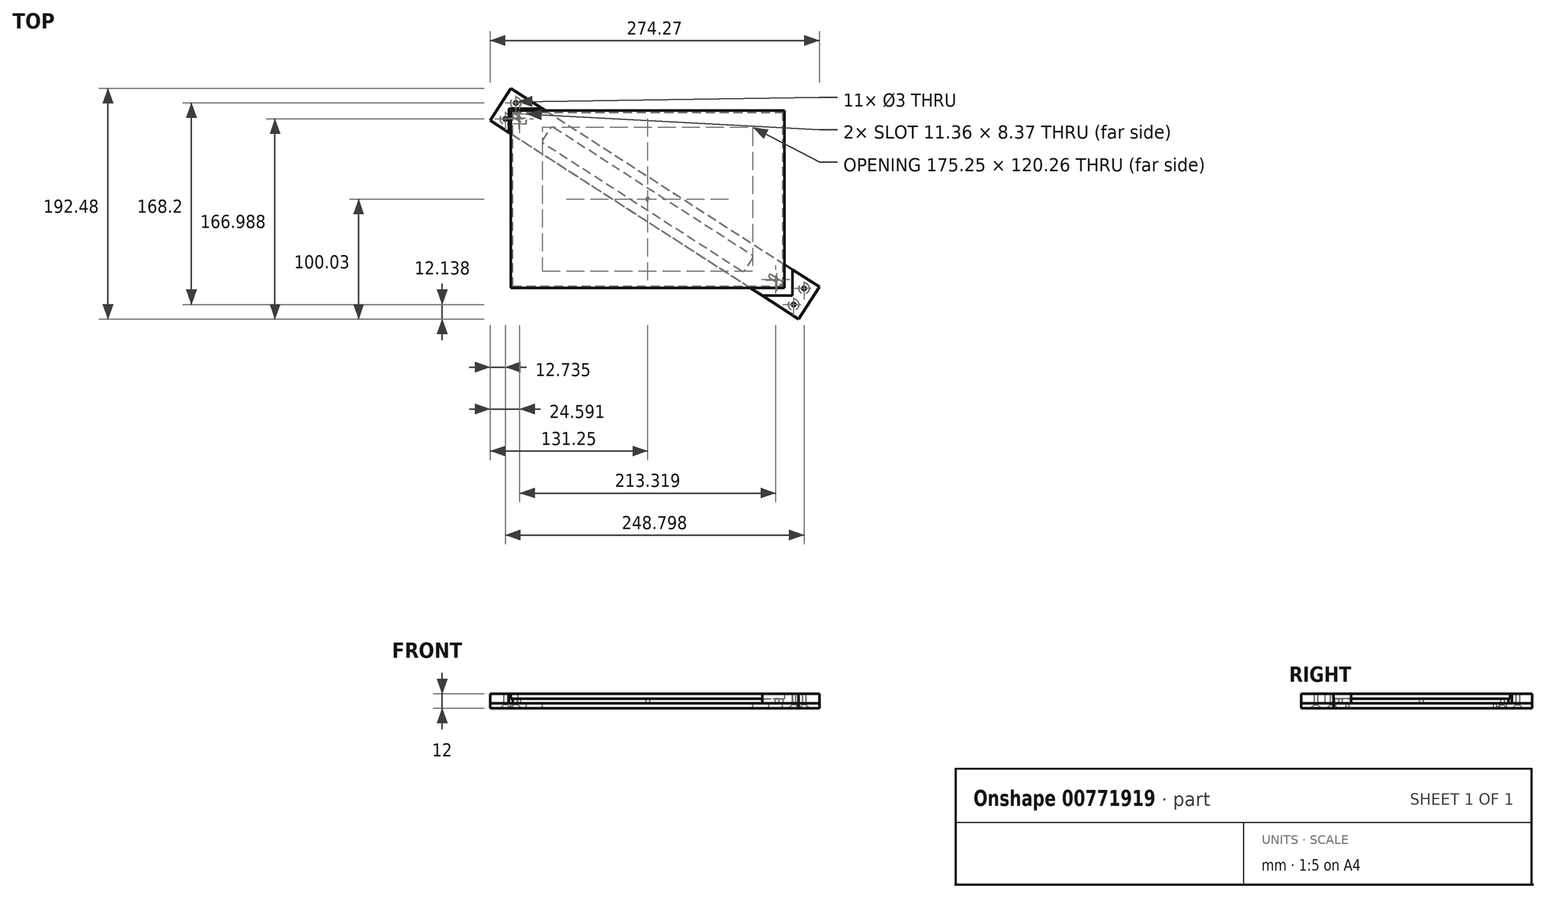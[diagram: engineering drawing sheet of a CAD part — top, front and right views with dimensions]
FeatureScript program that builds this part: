
annotation { "Feature Type Name" : "Feature", "Feature Type Description" : "" }
export const myFeature = defineFeature(function(context is Context, id is Id, definition is map)
    precondition{}
    {
        {
            assignVariable(context, id + "F0", {"name" : "printPlateThickness", "anyValue" : 4 * mm});
        }
        {
            var Q0;
            Q0=qCreatedBy(makeId("Top.planeOp"),FACE);
            var sketch = newSketch(context, id + "F1", { "sketchPlane" : qUnion([Q0])});
            skLineSegment(sketch, "E0.bottom", {"start": v(0, 0) * mm, "end": v(225, 0) * mm});
            skLineSegment(sketch, "E0.top", {"start": v(0, 145) * mm, "end": v(225, 145) * mm});
            skLineSegment(sketch, "E0.left", {"start": v(0, 0) * mm, "end": v(0, 145) * mm});
            skLineSegment(sketch, "E0.right", {"start": v(225, 0) * mm, "end": v(225, 145) * mm});
            skCircle(sketch, "E1", {"center": v(5, 140) * mm, "radius": 1.5 * mm});
            skCircle(sketch, "E2", {"center": v(220, 5) * mm, "radius": 1.5 * mm});
            skLineSegment(sketch, "E3.bottom", {"start": v(-1.5, 146.5) * mm, "end": v(226.5, 146.5) * mm});
            skLineSegment(sketch, "E3.top", {"start": v(-1.5, -1.5) * mm, "end": v(226.5, -1.5) * mm});
            skLineSegment(sketch, "E3.left", {"start": v(-1.5, 146.5) * mm, "end": v(-1.5, -1.5) * mm});
            skLineSegment(sketch, "E3.right", {"start": v(226.5, 146.5) * mm, "end": v(226.5, -1.5) * mm});
            skLineSegment(sketch, "E4", {"start": v(0, 0) * mm, "end": v(225, 145) * mm, "construction": true});
            skLineSegment(sketch, "E5", {"start": v(0, 145) * mm, "end": v(225, 0) * mm, "construction": true});
            skCircle(sketch, "E6", {"center": v(112.5, 72.5) * mm, "radius": 1.5 * mm});
            skSolve(sketch);
        }
        {
            var Q0;
            Q0=makeQuery(id+"F1.imprint","IMPRINT",FACE,{"disambiguationData":[TD([[makeQuery(id+"F1.imprint","IMPRINT",EDGE,{"derivedFrom":sQuery(id+"F1.wireOp",EDGE,"E0.bottom")}),1.0]])]});
            extrude(context, id + "F2", {"entities" : qUnion([Q0]), "depth" : getVariable(context, 'printPlateThickness'), "offsetDistance" : 25 * mm});
        }
        {
            var Q0;
            Q0=qCreatedBy(makeId("Top.planeOp"),FACE);
            var sketch = newSketch(context, id + "F3", { "sketchPlane" : qUnion([Q0])});
            skLineSegment(sketch, "E7", {"start": v(0, 145) * mm, "end": v(225, 0) * mm, "construction": true});
            skLineSegment(sketch, "E8", {"start": v(225, 0) * mm, "end": v(246.85, -14.08) * mm, "construction": true});
            skLineSegment(sketch, "E9", {"start": v(0, 145) * mm, "end": v(-10.09, 151.5) * mm, "construction": true});
            skLineSegment(sketch, "E10", {"start": v(-18.75, 138.05) * mm, "end": v(-1.42, 164.95) * mm});
            skLineSegment(sketch, "E11", {"start": v(-1.42, 164.95) * mm, "end": v(255.52, -0.64) * mm});
            skLineSegment(sketch, "E12", {"start": v(255.52, -0.64) * mm, "end": v(238.19, -27.53) * mm});
            skLineSegment(sketch, "E13", {"start": v(238.19, -27.53) * mm, "end": v(-18.75, 138.05) * mm});
            skCircle(sketch, "E14", {"center": v(2.65, 152.8) * mm, "radius": 1.5 * mm});
            skCircle(sketch, "E15", {"center": v(-6.01, 139.36) * mm, "radius": 1.5 * mm});
            skCircle(sketch, "E16", {"center": v(234.12, -15.4) * mm, "radius": 1.5 * mm});
            skCircle(sketch, "E17", {"center": v(242.78, -1.94) * mm, "radius": 1.5 * mm});
            skLineSegment(sketch, "E18", {"start": v(5, 140) * mm, "end": v(45.54, 113.87) * mm, "construction": true});
            skLineSegment(sketch, "E19", {"start": v(175.06, 33.96) * mm, "end": v(220, 5) * mm, "construction": true});
            skLineSegment(sketch, "E20", {"start": v(220, 5) * mm, "end": v(229, -0.8) * mm, "construction": true});
            skLineSegment(sketch, "E21", {"start": v(5, 140) * mm, "end": v(-2.8, 145.03) * mm, "construction": true});
            skLineSegment(sketch, "E22", {"start": v(-1.9, 136.66) * mm, "end": v(3.2, 144.58) * mm, "construction": true});
            skLineSegment(sketch, "E23", {"start": v(11.96, 139.72) * mm, "end": v(6.4, 131.1) * mm, "construction": true});
            skCircle(sketch, "E24", {"center": v(1.64, 142.17) * mm, "radius": 1.5 * mm});
            skCircle(sketch, "E25", {"center": v(10.04, 136.75) * mm, "radius": 1.5 * mm});
            skLineSegment(sketch, "E26", {"start": v(2.45, 143.43) * mm, "end": v(10.86, 138.01) * mm});
            skLineSegment(sketch, "E27", {"start": v(0.83, 140.9) * mm, "end": v(9.23, 135.49) * mm});
            skLineSegment(sketch, "E28", {"start": v(217.61, 12.37) * mm, "end": v(212.26, 4.07) * mm, "construction": true});
            skLineSegment(sketch, "E29", {"start": v(226.04, 6.99) * mm, "end": v(221.04, -0.77) * mm, "construction": true});
            skCircle(sketch, "E30", {"center": v(214.96, 8.25) * mm, "radius": 1.5 * mm});
            skCircle(sketch, "E31", {"center": v(223.36, 2.83) * mm, "radius": 1.5 * mm});
            skLineSegment(sketch, "E32", {"start": v(215.77, 9.51) * mm, "end": v(224.17, 4.1) * mm});
            skLineSegment(sketch, "E33", {"start": v(214.14, 6.99) * mm, "end": v(222.55, 1.57) * mm});
            skLineSegment(sketch, "E34", {"start": v(34.46, 132.31) * mm, "end": v(199.2, 26.14) * mm});
            skLineSegment(sketch, "E35", {"start": v(199.8, 23.37) * mm, "end": v(193.3, 13.29) * mm});
            skLineSegment(sketch, "E36", {"start": v(190.54, 12.69) * mm, "end": v(25.8, 118.86) * mm});
            skLineSegment(sketch, "E37", {"start": v(25.2, 121.63) * mm, "end": v(31.7, 131.71) * mm});
            skPoint(sketch, "E38.visualSharp", {"position": v(32.78, 133.4) * mm});
            skArc(sketch, "E38.filletArc", {"start": v(34.46, 132.31) * mm, "mid": v(32.95, 132.58) * mm, "end": v(31.7, 131.71) * mm});
            skPoint(sketch, "E39.visualSharp", {"position": v(24.1, 119.95) * mm});
            skArc(sketch, "E39.filletArc", {"start": v(25.2, 121.63) * mm, "mid": v(24.92, 120.12) * mm, "end": v(25.8, 118.86) * mm});
            skPoint(sketch, "E40.visualSharp", {"position": v(192.22, 11.6) * mm});
            skArc(sketch, "E40.filletArc", {"start": v(190.54, 12.69) * mm, "mid": v(192.05, 12.42) * mm, "end": v(193.3, 13.29) * mm});
            skPoint(sketch, "E41.visualSharp", {"position": v(200.9, 25.05) * mm});
            skArc(sketch, "E41.filletArc", {"start": v(199.8, 23.37) * mm, "mid": v(200.08, 24.88) * mm, "end": v(199.2, 26.14) * mm});
            skSolve(sketch);
        }
        {
            var Q0;
            Q0 = qSketchRegion(id + "F3", true);
            extrude(context, id + "F4", {"entities" : qUnion([Q0]), "oppositeDirection" : true, "depth" : 4 * mm, "offsetDistance" : 25 * mm});
        }
        {
            var Q0;
            Q0=makeQuery(id+"F4.opExtrude","CAP_FACE",FACE,{"disambiguationData":[OSD([sQuery(id+"F3.wireOp",EDGE,"E10"),sQuery(id+"F3.wireOp",EDGE,"E11"),sQuery(id+"F3.wireOp",EDGE,"E12"),sQuery(id+"F3.wireOp",EDGE,"E13"),sQuery(id+"F3.wireOp",EDGE,"E14"),sQuery(id+"F3.wireOp",EDGE,"E15"),sQuery(id+"F3.wireOp",EDGE,"E16"),sQuery(id+"F3.wireOp",EDGE,"E17"),sQuery(id+"F3.wireOp",EDGE,"E24"),sQuery(id+"F3.wireOp",EDGE,"E25"),sQuery(id+"F3.wireOp",EDGE,"E26"),sQuery(id+"F3.wireOp",EDGE,"E27"),sQuery(id+"F3.wireOp",EDGE,"E30"),sQuery(id+"F3.wireOp",EDGE,"E31"),sQuery(id+"F3.wireOp",EDGE,"E32"),sQuery(id+"F3.wireOp",EDGE,"E33")])],"isStart":true});
            var sketch = newSketch(context, id + "F5", { "sketchPlane" : qUnion([Q0])});
            skLineSegment(sketch, "E42", {"start": v(-1.42, 164.95) * mm, "end": v(24.88, 148) * mm});
            skLineSegment(sketch, "E43", {"start": v(24.88, 148) * mm, "end": v(-3, 148) * mm});
            skLineSegment(sketch, "E44", {"start": v(-3, 148) * mm, "end": v(-3, 127.9) * mm});
            skLineSegment(sketch, "E45", {"start": v(-3, 127.9) * mm, "end": v(-18.75, 138.05) * mm});
            skLineSegment(sketch, "E46", {"start": v(-18.75, 138.05) * mm, "end": v(-1.42, 164.95) * mm});
            skLineSegment(sketch, "E47", {"start": v(233, 13.88) * mm, "end": v(255.52, -0.64) * mm});
            skLineSegment(sketch, "E48", {"start": v(255.52, -0.64) * mm, "end": v(238.19, -27.53) * mm});
            skLineSegment(sketch, "E49", {"start": v(238.19, -27.53) * mm, "end": v(207.88, -8) * mm});
            skLineSegment(sketch, "E50", {"start": v(207.88, -8) * mm, "end": v(233, -8) * mm});
            skLineSegment(sketch, "E51", {"start": v(233, -8) * mm, "end": v(233, 13.88) * mm});
            skCircle(sketch, "E52", {"center": v(242.78, -1.94) * mm, "radius": 1.25 * mm});
            skCircle(sketch, "E53", {"center": v(234.12, -15.4) * mm, "radius": 1.25 * mm});
            skCircle(sketch, "E54", {"center": v(2.65, 152.8) * mm, "radius": 1.25 * mm});
            skCircle(sketch, "E55", {"center": v(-6.01, 139.36) * mm, "radius": 1.25 * mm});
            skSolve(sketch);
        }
        {
            var Q0;
            Q0=makeQuery(id+"F5.imprint","IMPRINT",FACE,{"disambiguationData":[TD([[makeQuery(id+"F5.imprint","IMPRINT",EDGE,{"derivedFrom":sQuery(id+"F5.wireOp",EDGE,"E42")}),-1.0]])]});
            extrude(context, id + "F6", {"entities" : qUnion([Q0]), "depth" : 8 * mm, "offsetDistance" : 25 * mm});
        }
        {
            var Q0;
            Q0=makeQuery(id+"F5.imprint","IMPRINT",FACE,{"disambiguationData":[TD([[makeQuery(id+"F5.imprint","IMPRINT",EDGE,{"derivedFrom":sQuery(id+"F5.wireOp",EDGE,"E47")}),-1.0]])]});
            extrude(context, id + "F7", {"entities" : qUnion([Q0]), "depth" : 8 * mm, "offsetDistance" : 25 * mm});
        }
        {
            var Q0;
            Q0=makeQuery(id+"F1.imprint","IMPRINT",FACE,{"disambiguationData":[TD([[makeQuery(id+"F1.imprint","IMPRINT",EDGE,{"derivedFrom":sQuery(id+"F1.wireOp",EDGE,"E0.bottom")}),1.0]])]});
            var Q1;
            Q1=makeQuery(id+"F1.imprint","IMPRINT",FACE,{"disambiguationData":[TD([[makeQuery(id+"F1.imprint","IMPRINT",EDGE,{"derivedFrom":sQuery(id+"F1.wireOp",EDGE,"E0.bottom")}),-1.0]])]});
            var Q2;
            Q2=makeQuery(id+"F1.imprint","IMPRINT",FACE,{"disambiguationData":[TD([[makeQuery(id+"F1.imprint","IMPRINT",EDGE,{"derivedFrom":sQuery(id+"F1.wireOp",EDGE,"E1")}),1.0]])]});
            var Q3;
            Q3=makeQuery(id+"F1.imprint","IMPRINT",FACE,{"disambiguationData":[TD([[makeQuery(id+"F1.imprint","IMPRINT",EDGE,{"derivedFrom":sQuery(id+"F1.wireOp",EDGE,"E2")}),1.0]])]});
            var Q4;
            Q4=makeQuery(id+"F1.imprint","IMPRINT",FACE,{"disambiguationData":[TD([[makeQuery(id+"F1.imprint","IMPRINT",EDGE,{"derivedFrom":sQuery(id+"F1.wireOp",EDGE,"E6")}),1.0]])]});
            extrude(context, id + "F8", {"entities" : qUnion([Q0, Q1, Q2, Q3, Q4]), "depth" : 4 * mm + getVariable(context, 'printPlateThickness'), "offsetDistance" : 25 * mm, "hasSecondDirection" : true, "secondDirectionOppositeDirection" : false, "secondDirectionDepth" : getVariable(context, 'printPlateThickness')});
        }
        {
            var Q0;
            Q0=makeQuery(id+"F4.opExtrude","CAP_EDGE",EDGE,{"disambiguationData":[OSD([sQuery(id+"F3.wireOp",EDGE,"E16")])],"isStart":false});
            var Q1;
            Q1=makeQuery(id+"F4.opExtrude","CAP_EDGE",EDGE,{"disambiguationData":[OSD([sQuery(id+"F3.wireOp",EDGE,"E17")])],"isStart":false});
            var Q2;
            Q2=makeQuery(id+"F4.opExtrude","CAP_EDGE",EDGE,{"disambiguationData":[OSD([sQuery(id+"F3.wireOp",EDGE,"E14")])],"isStart":false});
            var Q3;
            Q3=makeQuery(id+"F4.opExtrude","CAP_EDGE",EDGE,{"disambiguationData":[OSD([sQuery(id+"F3.wireOp",EDGE,"E15")])],"isStart":false});
            chamfer(context, id + "F9", {"entities" : qUnion([Q0, Q1, Q2, Q3]), "width" : 3 * mm, "tangentPropagation" : true});
        }
    });
